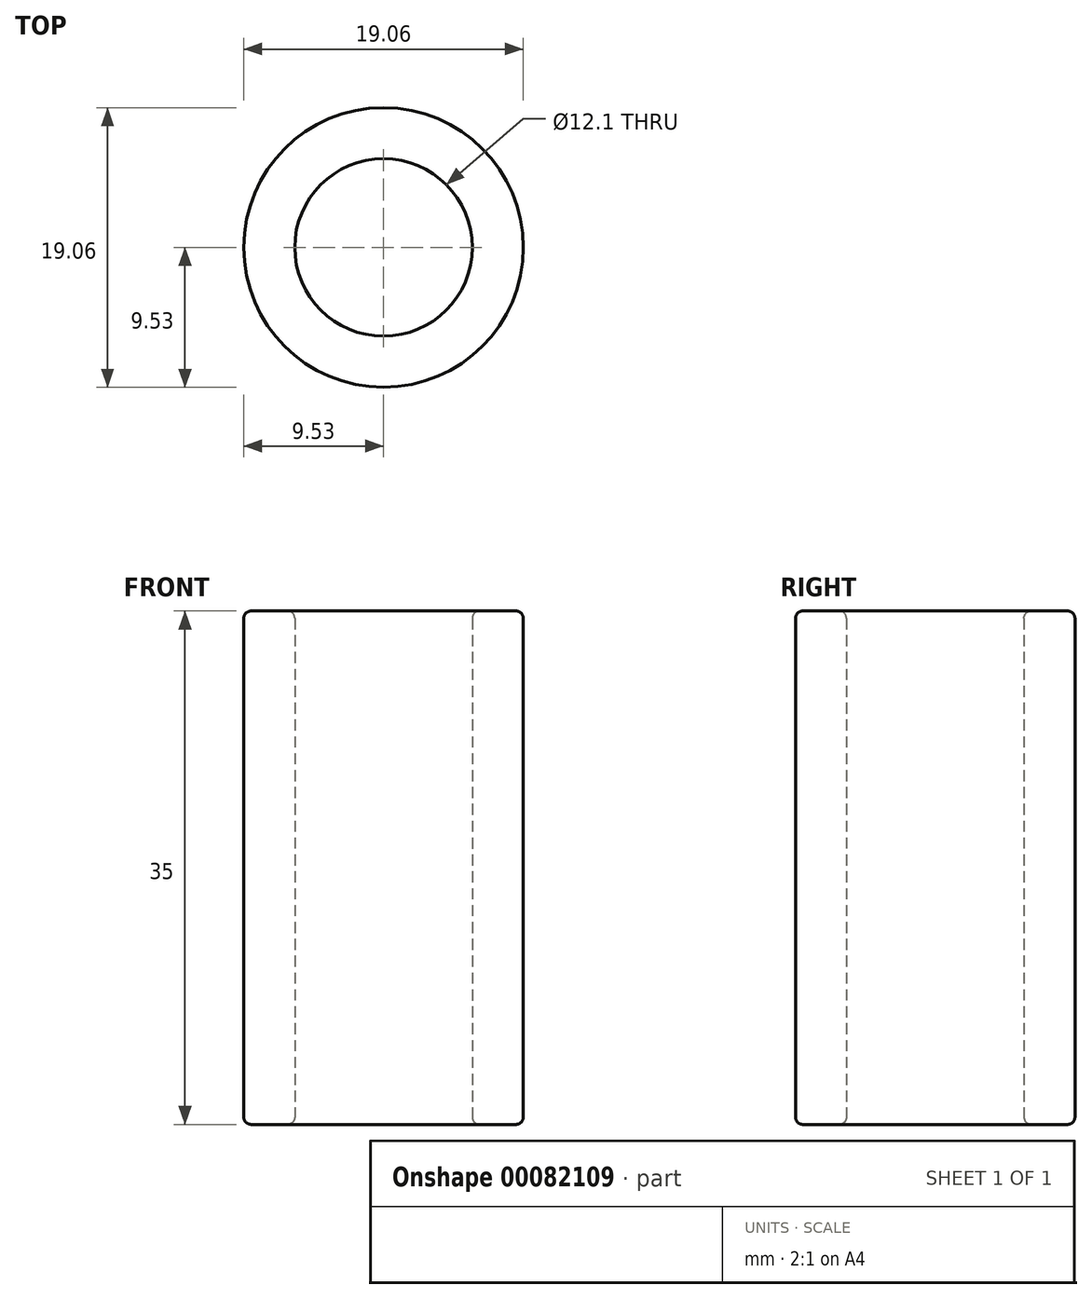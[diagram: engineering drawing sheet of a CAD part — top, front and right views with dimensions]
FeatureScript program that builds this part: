
annotation { "Feature Type Name" : "Feature", "Feature Type Description" : "" }
export const myFeature = defineFeature(function(context is Context, id is Id, definition is map)
    precondition{}
    {
        {
            var Q0;
            Q0=qCreatedBy(makeId("Top.planeOp"),FACE);
            var sketch = newSketch(context, id + "F0", { "sketchPlane" : qUnion([Q0])});
            skCircle(sketch, "E0", {"center": v(0, 0) * mm, "radius": 9.53 * mm});
            skCircle(sketch, "E1", {"center": v(0, 0) * mm, "radius": 6.05 * mm});
            skSolve(sketch);
        }
        {
            var Q0;
            Q0 = qSketchRegion(id + "F0", true);
            extrude(context, id + "F1", {"entities" : qUnion([Q0]), "depth" : 35 * mm});
        }
        {
            var Q0;
            Q0=makeQuery(id+"F1.opExtrude","CAP_FACE",FACE,{"disambiguationData":[OSD([sQuery(id+"F0.wireOp",EDGE,"E0"),sQuery(id+"F0.wireOp",EDGE,"E1")])],"isStart":false});
            var Q1;
            Q1=makeQuery(id+"F1.opExtrude","CAP_FACE",FACE,{"disambiguationData":[OSD([sQuery(id+"F0.wireOp",EDGE,"E0"),sQuery(id+"F0.wireOp",EDGE,"E1")])],"isStart":true});
            fillet(context, id + "F2", {"entities" : qUnion([Q0, Q1]), "radius" : 0.5 * mm, "tangentPropagation" : true, "allowEdgeOverflow" : false});
        }
    });
